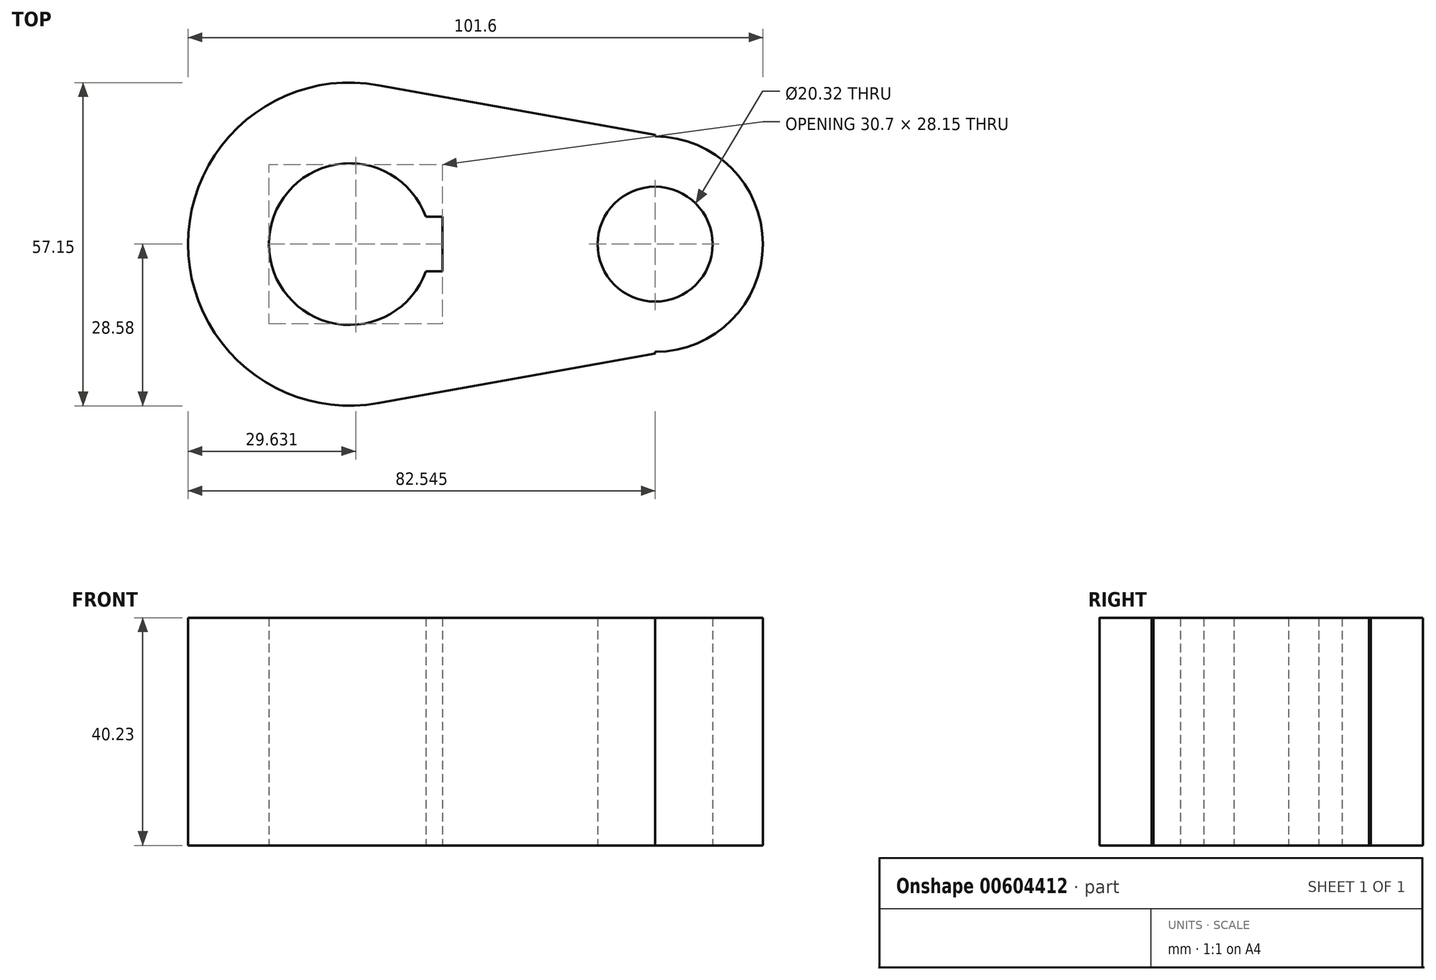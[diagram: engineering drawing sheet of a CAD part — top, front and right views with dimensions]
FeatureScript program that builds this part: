
annotation { "Feature Type Name" : "Feature", "Feature Type Description" : "" }
export const myFeature = defineFeature(function(context is Context, id is Id, definition is map)
    precondition{}
    {
        {
            var Q0;
            Q0=qCreatedBy(makeId("Top.planeOp"),FACE);
            var sketch = newSketch(context, id + "F0", { "sketchPlane" : qUnion([Q0])});
            skCircle(sketch, "E0", {"center": v(0, 0) * mm, "radius": 28.58 * mm});
            skArc(sketch, "E1", {"start": v(13.45, 4.83) * mm, "mid": v(-14.29, 0) * mm, "end": v(13.45, -4.83) * mm});
            skCircle(sketch, "E2", {"center": v(53.98, 0) * mm, "radius": 10.16 * mm});
            skArc(sketch, "E3", {"start": v(54, -19.05) * mm, "mid": v(73.03, 0) * mm, "end": v(54, 19.05) * mm});
            skLineSegment(sketch, "E4", {"start": v(0, -29.03) * mm, "end": v(54, -19.35) * mm});
            skLineSegment(sketch, "E5", {"start": v(54, -19.35) * mm, "end": v(54, -19.05) * mm});
            skLineSegment(sketch, "E6.trimOffspring", {"start": v(54, 19.05) * mm, "end": v(54, 19.35) * mm});
            skLineSegment(sketch, "E7", {"start": v(54, 19.35) * mm, "end": v(0, 29.03) * mm});
            skLineSegment(sketch, "E8.bottom", {"start": v(16.4, 4.83) * mm, "end": v(13.45, 4.83) * mm});
            skLineSegment(sketch, "E8.top", {"start": v(16.4, -4.83) * mm, "end": v(13.45, -4.83) * mm});
            skLineSegment(sketch, "E8.left", {"start": v(16.4, 4.83) * mm, "end": v(16.4, -4.83) * mm});
            skSolve(sketch);
        }
        {
            var Q0;
            Q0 = qSketchRegion(id + "F0", true);
            extrude(context, id + "F1", {"entities" : qUnion([Q0]), "depth" : 40.23 * mm, "offsetDistance" : 25.4 * mm});
        }
    });
